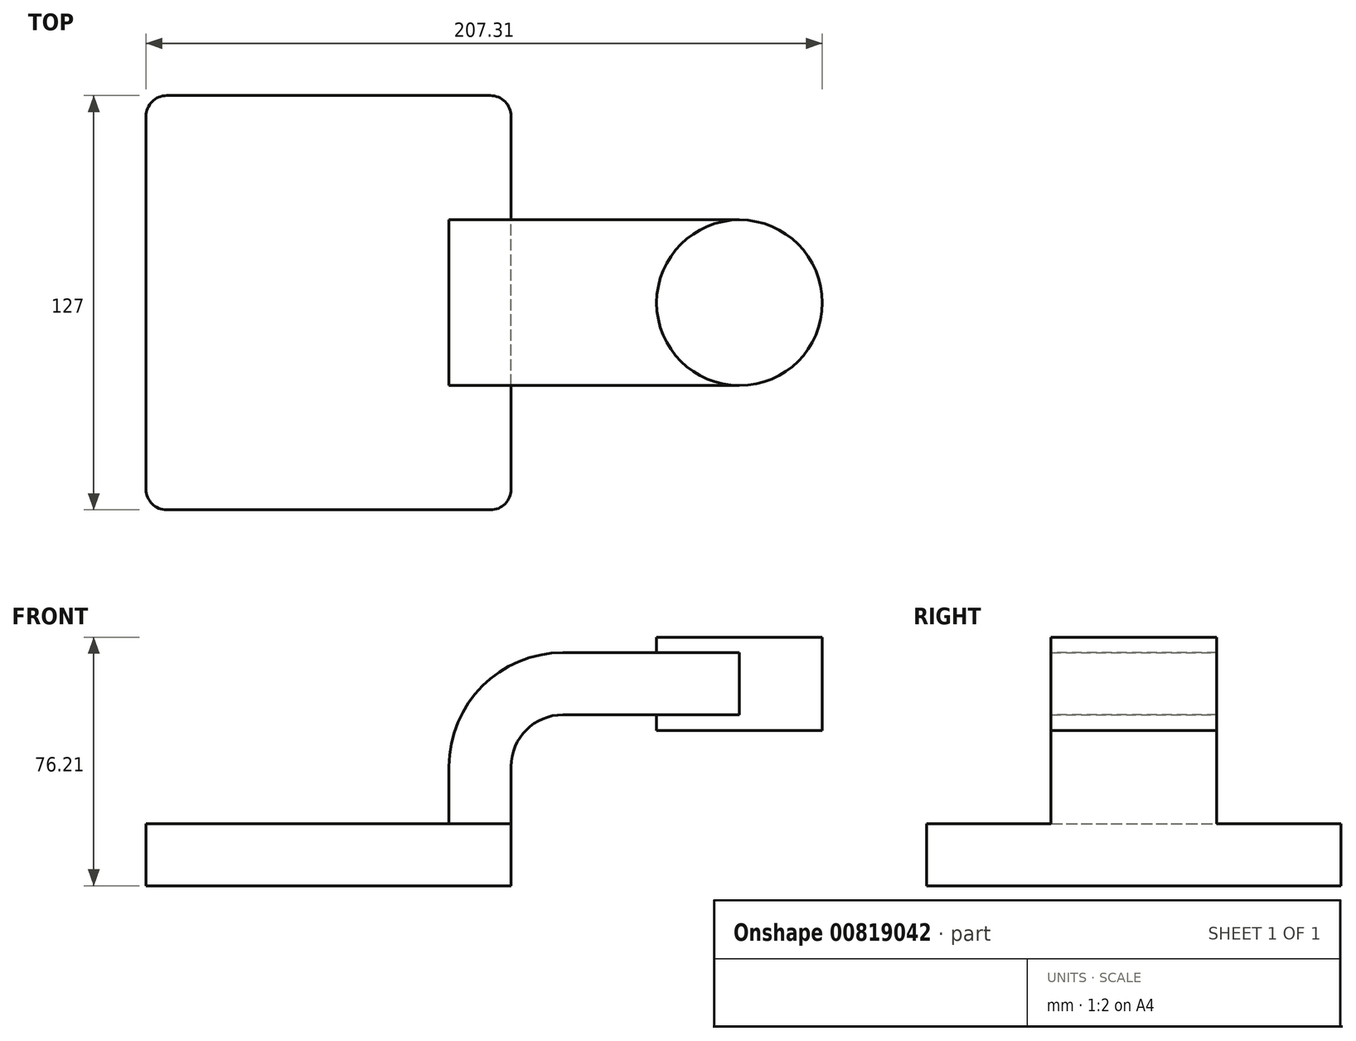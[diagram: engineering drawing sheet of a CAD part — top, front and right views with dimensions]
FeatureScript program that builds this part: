
annotation { "Feature Type Name" : "Feature", "Feature Type Description" : "" }
export const myFeature = defineFeature(function(context is Context, id is Id, definition is map)
    precondition{}
    {
        {
            var Q0;
            Q0=qCreatedBy(makeId("Front.planeOp"),FACE);
            var sketch = newSketch(context, id + "F0", { "sketchPlane" : qUnion([Q0])});
            skLineSegment(sketch, "E0.bottom", {"start": v(-55.96, 9.52) * mm, "end": v(55.96, 9.53) * mm});
            skLineSegment(sketch, "E0.top", {"start": v(-55.96, -9.53) * mm, "end": v(55.96, -9.53) * mm});
            skLineSegment(sketch, "E0.left", {"start": v(-55.96, 9.52) * mm, "end": v(-55.96, -9.53) * mm});
            skLineSegment(sketch, "E0.right", {"start": v(55.96, 9.53) * mm, "end": v(55.96, -9.52) * mm});
            skPoint(sketch, "E0.middle", {"position": v(0, 0) * mm});
            skLineSegment(sketch, "E1.bottom", {"start": v(100.55, 38.1) * mm, "end": v(151.35, 38.1) * mm});
            skLineSegment(sketch, "E1.top", {"start": v(100.55, 66.67) * mm, "end": v(151.35, 66.67) * mm});
            skLineSegment(sketch, "E1.left", {"start": v(100.55, 38.1) * mm, "end": v(100.55, 66.67) * mm});
            skLineSegment(sketch, "E1.right", {"start": v(151.35, 38.1) * mm, "end": v(151.35, 66.67) * mm});
            skPoint(sketch, "E1.middle", {"position": v(125.95, 52.39) * mm});
            skLineSegment(sketch, "E2", {"start": v(55.96, 9.53) * mm, "end": v(55.96, 27) * mm});
            skArc(sketch, "E3", {"start": v(55.96, 27) * mm, "mid": v(60.6, 38.23) * mm, "end": v(71.83, 42.88) * mm});
            skLineSegment(sketch, "E4", {"start": v(71.83, 42.88) * mm, "end": v(125.92, 42.88) * mm});
            skLineSegment(sketch, "E5.0", {"start": v(71.83, 61.93) * mm, "end": v(125.92, 61.93) * mm});
            skArc(sketch, "E5.1", {"start": v(36.9, 27) * mm, "mid": v(47.14, 51.7) * mm, "end": v(71.83, 61.93) * mm});
            skLineSegment(sketch, "E5.2", {"start": v(36.9, 9.53) * mm, "end": v(36.9, 27) * mm});
            skFitSpline(sketch, "E6", {"points": [v(-55.96, 9.52) * mm, v(71.83, 61.93) * mm], "startDerivative": vector(38.18, 156.56) * mm, "endDerivative": vector(164.5, -51.73) * mm});
            skLineSegment(sketch, "E7", {"start": v(125.92, 61.93) * mm, "end": v(125.92, 42.88) * mm});
            skLineSegment(sketch, "E8", {"start": v(125.95, 66.67) * mm, "end": v(125.95, 38.1) * mm});
            skSolve(sketch);
        }
        {
            var Q0;
            Q0=makeQuery(id+"F0.imprint","IMPRINT",FACE,{"disambiguationData":[TD([[makeQuery(id+"F0.imprint","IMPRINT",EDGE,{"derivedFrom":sQuery(id+"F0.wireOp",EDGE,"E0.top")}),1.0]])]});
            extrude(context, id + "F1", {"entities" : qUnion([Q0]), "endBound" : BoundingType.SYMMETRIC, "depth" : 127 * mm, "offsetDistance" : 25.4 * mm});
        }
        {
            var Q0;
            {var subQ1=sQuery(id+"F0.wireOp",EDGE,"E2");Q0=makeQuery(id+"F0.imprint","IMPRINT",FACE,{"disambiguationData":[TD([[makeQuery(id+"F0.imprint","IMPRINT",EDGE,{"derivedFrom":subQ1}),1.0]])]});}
            var Q1;
            {var subQ5=sQuery(id+"F0.wireOp",EDGE,"E7");Q1=makeQuery(id+"F0.imprint","IMPRINT",FACE,{"disambiguationData":[TD([[makeQuery(id+"F0.imprint","IMPRINT",EDGE,{"derivedFrom":subQ5}),-1.0]])]});}
            extrude(context, id + "F2", {"entities" : qUnion([Q0, Q1]), "operationType" : NewBodyOperationType.ADD, "endBound" : BoundingType.SYMMETRIC, "depth" : 50.8 * mm, "offsetDistance" : 25.4 * mm});
        }
        {
            var Q0;
            Q0=makeQuery(id+"F0.imprint","IMPRINT",FACE,{"disambiguationData":[TD([[makeQuery(id+"F0.imprint","IMPRINT",EDGE,{"derivedFrom":sQuery(id+"F0.wireOp",EDGE,"E5.1")}),1.0]])]});
            extrude(context, id + "F3", {"entities" : qUnion([Q0]), "operationType" : NewBodyOperationType.ADD, "endBound" : BoundingType.SYMMETRIC, "depth" : 15.88 * mm, "offsetDistance" : 25.4 * mm});
        }
        {
            var Q0;
            {var subQ0=sQuery(id+"F0.wireOp",EDGE,"E1.right");Q0=makeQuery(id+"F0.imprint","IMPRINT",FACE,{"disambiguationData":[TD([[makeQuery(id+"F0.imprint","IMPRINT",EDGE,{"derivedFrom":subQ0}),1.0]])]});}
            var Q1;
            Q1=sQuery(id+"F0.wireOp",EDGE,"E8");
            revolve(context, id + "F4", {"operationType" : NewBodyOperationType.ADD, "surfaceOperationType" : NewSurfaceOperationType.NEW, "entities" : qUnion([Q0]), "axis" : qUnion([Q1]), "revolveType" : RevolveType.FULL});
        }
        {
            var Q0;
            Q0=makeQuery(id+"F1.opExtrude","CAP_EDGE",EDGE,{"disambiguationData":[OSD([sQuery(id+"F0.wireOp",EDGE,"E0.left")])],"isStart":false});
            var Q1;
            Q1=makeQuery(id+"F1.opExtrude","CAP_EDGE",EDGE,{"disambiguationData":[OSD([sQuery(id+"F0.wireOp",EDGE,"E0.right")])],"isStart":false});
            var Q2;
            Q2=makeQuery(id+"F1.opExtrude","CAP_EDGE",EDGE,{"disambiguationData":[OSD([sQuery(id+"F0.wireOp",EDGE,"E0.right")])],"isStart":true});
            var Q3;
            Q3=makeQuery(id+"F1.opExtrude","CAP_EDGE",EDGE,{"disambiguationData":[OSD([sQuery(id+"F0.wireOp",EDGE,"E0.left")])],"isStart":true});
            fillet(context, id + "F5", {"entities" : qUnion([Q0, Q1, Q2, Q3]), "radius" : 6.35 * mm, "tangentPropagation" : true, "allowEdgeOverflow" : false});
        }
    });
